# Revit family: F100G
name_source: partatom
category: Windows
revit_build: Autodesk Revit 2014 (Build: 20130308_1515(x64)
units: mm (PartAtom-declared; Revit-internal decimal feet)

## types (75) — shared parameters
Analytic Construction = <None>
Main Material = Lamilux-White
Secondary Material = Lamilux- Glass
With Operator = Yes

## per-type parameters (varying)
| type | Kurb Height | Length | Pitched Roof | Width |
| 600X600X500 | 500 mm  [stored 1.64042 ft] | 600 mm  [stored 1.9685 ft] | No | 600 mm  [stored 1.9685 ft] |
| 600X600X400 | 400 mm  [stored 1.31234 ft] | 600 mm  [stored 1.9685 ft] | No | 600 mm  [stored 1.9685 ft] |
| 600X600X300 | 300 mm  [stored 0.984252 ft] | 600 mm  [stored 1.9685 ft] | No | 600 mm  [stored 1.9685 ft] |
| 600X600X150 | 150 mm | 600 mm  [stored 1.9685 ft] | No | 600 mm  [stored 1.9685 ft] |
| 600X600X400_Pitched | 400 mm  [stored 1.31234 ft] | 600 mm  [stored 1.9685 ft] | Yes | 600 mm  [stored 1.9685 ft] |
| 600X900X500 | 500 mm  [stored 1.64042 ft] | 900 mm  [stored 2.95276 ft] | No | 600 mm  [stored 1.9685 ft] |
| 600X900X400 | 400 mm  [stored 1.31234 ft] | 900 mm  [stored 2.95276 ft] | No | 600 mm  [stored 1.9685 ft] |
| 600X900X300 | 300 mm  [stored 0.984252 ft] | 900 mm  [stored 2.95276 ft] | No | 600 mm  [stored 1.9685 ft] |
| 600X900X150 | 150 mm | 900 mm  [stored 2.95276 ft] | No | 600 mm  [stored 1.9685 ft] |
| 600X900X400_Pitched | 400 mm  [stored 1.31234 ft] | 900 mm  [stored 2.95276 ft] | Yes | 600 mm  [stored 1.9685 ft] |
| 600X1200X500 | 500 mm  [stored 1.64042 ft] | 1200 mm | No | 600 mm  [stored 1.9685 ft] |
| 600X1200X300 | 300 mm  [stored 0.984252 ft] | 1200 mm | No | 600 mm  [stored 1.9685 ft] |
| 600X1200X150 | 150 mm | 1200 mm | No | 600 mm  [stored 1.9685 ft] |
| 600X1200X400_Pitched | 400 mm  [stored 1.31234 ft] | 1200 mm | Yes | 600 mm  [stored 1.9685 ft] |
| 700X1350X500 | 500 mm  [stored 1.64042 ft] | 1350 mm  [stored 4.42913 ft] | No | 700 mm  [stored 2.29659 ft] |
| 700X1350X400 | 400 mm  [stored 1.31234 ft] | 1350 mm  [stored 4.42913 ft] | No | 700 mm  [stored 2.29659 ft] |
| 700X1350X300 | 300 mm  [stored 0.984252 ft] | 1350 mm  [stored 4.42913 ft] | No | 700 mm  [stored 2.29659 ft] |
| 700X1350X150 | 150 mm | 1350 mm  [stored 4.42913 ft] | No | 700 mm  [stored 2.29659 ft] |
| 700X1350X400_Pitched | 400 mm  [stored 1.31234 ft] | 1350 mm  [stored 4.42913 ft] | Yes | 700 mm  [stored 2.29659 ft] |
| 800X800X500 | 500 mm  [stored 1.64042 ft] | 800 mm  [stored 2.62467 ft] | No | 800 mm  [stored 2.62467 ft] |
| 800X800X400 | 400 mm  [stored 1.31234 ft] | 800 mm  [stored 2.62467 ft] | No | 800 mm  [stored 2.62467 ft] |
| 800X800X300 | 300 mm  [stored 0.984252 ft] | 800 mm  [stored 2.62467 ft] | No | 800 mm  [stored 2.62467 ft] |
| 800X800X150 | 150 mm | 800 mm  [stored 2.62467 ft] | No | 800 mm  [stored 2.62467 ft] |
| 800X800X400_Pitched | 400 mm  [stored 1.31234 ft] | 800 mm  [stored 2.62467 ft] | Yes | 800 mm  [stored 2.62467 ft] |
| 800X1500X500 | 500 mm  [stored 1.64042 ft] | 1500 mm  [stored 4.92126 ft] | No | 800 mm  [stored 2.62467 ft] |
| 800X1500X400 | 400 mm  [stored 1.31234 ft] | 1500 mm  [stored 4.92126 ft] | No | 800 mm  [stored 2.62467 ft] |
| 800X1500X300 | 300 mm  [stored 0.984252 ft] | 1500 mm  [stored 4.92126 ft] | No | 800 mm  [stored 2.62467 ft] |
| 800X1500X150 | 150 mm | 1500 mm  [stored 4.92126 ft] | No | 800 mm  [stored 2.62467 ft] |
| 800X1500X400_Pitched | 400 mm  [stored 1.31234 ft] | 1500 mm  [stored 4.92126 ft] | Yes | 800 mm  [stored 2.62467 ft] |
| 900X900X500 | 500 mm  [stored 1.64042 ft] | 900 mm  [stored 2.95276 ft] | No | 900 mm  [stored 2.95276 ft] |
| 900X900X400 | 400 mm  [stored 1.31234 ft] | 900 mm  [stored 2.95276 ft] | No | 900 mm  [stored 2.95276 ft] |
| 900X900X300 | 300 mm  [stored 0.984252 ft] | 900 mm  [stored 2.95276 ft] | No | 900 mm  [stored 2.95276 ft] |
| 900X900X150 | 150 mm | 900 mm  [stored 2.95276 ft] | No | 900 mm  [stored 2.95276 ft] |
| 900X900X400_Pitched | 400 mm  [stored 1.31234 ft] | 900 mm  [stored 2.95276 ft] | Yes | 900 mm  [stored 2.95276 ft] |
| 900X1200X500 | 500 mm  [stored 1.64042 ft] | 1200 mm | No | 900 mm  [stored 2.95276 ft] |
| 900X1200X400 | 400 mm  [stored 1.31234 ft] | 1200 mm | No | 900 mm  [stored 2.95276 ft] |
| 900X1200X300 | 300 mm  [stored 0.984252 ft] | 1200 mm | No | 900 mm  [stored 2.95276 ft] |
| 900X1200X150 | 150 mm | 1200 mm | No | 900 mm  [stored 2.95276 ft] |
| 900X1200X400_Pitched | 400 mm  [stored 1.31234 ft] | 1200 mm | Yes | 900 mm  [stored 2.95276 ft] |
| 900X1450X150 | 150 mm | 1450 mm  [stored 4.75722 ft] | No | 900 mm  [stored 2.95276 ft] |
| 900X1450X400_Pitched | 400 mm  [stored 1.31234 ft] | 1450 mm  [stored 4.75722 ft] | Yes | 900 mm  [stored 2.95276 ft] |
| 1000X1000X500 | 500 mm  [stored 1.64042 ft] | 1000 mm  [stored 3.28084 ft] | No | 1000 mm  [stored 3.28084 ft] |
| 1000X1000X400 | 400 mm  [stored 1.31234 ft] | 1000 mm  [stored 3.28084 ft] | No | 1000 mm  [stored 3.28084 ft] |
| 1000X1000X300 | 300 mm  [stored 0.984252 ft] | 1000 mm  [stored 3.28084 ft] | No | 1000 mm  [stored 3.28084 ft] |
| 1000X1000X150 | 150 mm | 1000 mm  [stored 3.28084 ft] | No | 1000 mm  [stored 3.28084 ft] |
| 1000X1000X400_Pitched | 400 mm  [stored 1.31234 ft] | 1000 mm  [stored 3.28084 ft] | Yes | 1000 mm  [stored 3.28084 ft] |
| 1000X1500X500 | 500 mm  [stored 1.64042 ft] | 1500 mm  [stored 4.92126 ft] | No | 1000 mm  [stored 3.28084 ft] |
| 1000X1500X400 | 400 mm  [stored 1.31234 ft] | 1500 mm  [stored 4.92126 ft] | No | 1000 mm  [stored 3.28084 ft] |
| 1000X1500X300 | 300 mm  [stored 0.984252 ft] | 1500 mm  [stored 4.92126 ft] | No | 1000 mm  [stored 3.28084 ft] |
| 1000X1500X150 | 150 mm | 1500 mm  [stored 4.92126 ft] | No | 1000 mm  [stored 3.28084 ft] |
| 1000X1500X400_Pitched | 400 mm  [stored 1.31234 ft] | 1500 mm  [stored 4.92126 ft] | Yes | 1000 mm  [stored 3.28084 ft] |
| 1200X1200X500 | 500 mm  [stored 1.64042 ft] | 1200 mm | No | 1200 mm |
| 1200X1200X400 | 400 mm  [stored 1.31234 ft] | 1200 mm | No | 1200 mm |
| 1200X1200X300 | 300 mm  [stored 0.984252 ft] | 1200 mm | No | 1200 mm |
| 1200X1200X150 | 150 mm | 1200 mm | No | 1200 mm |
| 1200X1200X400_Pitched | 400 mm  [stored 1.31234 ft] | 1200 mm | Yes | 1200 mm |
| 1200X1500X500 | 500 mm  [stored 1.64042 ft] | 1500 mm  [stored 4.92126 ft] | No | 1200 mm |
| 1200X1500X400 | 400 mm  [stored 1.31234 ft] | 1500 mm  [stored 4.92126 ft] | No | 1200 mm |
| 1200X1500X300 | 300 mm  [stored 0.984252 ft] | 1500 mm  [stored 4.92126 ft] | No | 1200 mm |
| 1200X1500X150 | 150 mm | 1500 mm  [stored 4.92126 ft] | No | 1200 mm |
| 1200X1500X400_Pitched | 400 mm  [stored 1.31234 ft] | 1500 mm  [stored 4.92126 ft] | Yes | 1200 mm |
| 1250X1250X500 | 500 mm  [stored 1.64042 ft] | 1250 mm  [stored 4.10105 ft] | No | 1250 mm  [stored 4.10105 ft] |
| 1250X1250X400 | 400 mm  [stored 1.31234 ft] | 1250 mm  [stored 4.10105 ft] | No | 1250 mm  [stored 4.10105 ft] |
| 1250X1250X300 | 300 mm  [stored 0.984252 ft] | 1250 mm  [stored 4.10105 ft] | No | 1250 mm  [stored 4.10105 ft] |
| 1250X1250X150 | 150 mm | 1250 mm  [stored 4.10105 ft] | No | 1250 mm  [stored 4.10105 ft] |
| 1250X1250X400_Pitched | 400 mm  [stored 1.31234 ft] | 1250 mm  [stored 4.10105 ft] | Yes | 1250 mm  [stored 4.10105 ft] |
| 1400X1400X500 | 500 mm  [stored 1.64042 ft] | 1400 mm  [stored 4.59318 ft] | No | 1400 mm  [stored 4.59318 ft] |
| 1400X1400X400 | 400 mm  [stored 1.31234 ft] | 1400 mm  [stored 4.59318 ft] | No | 1400 mm  [stored 4.59318 ft] |
| 1400X1400X300 | 300 mm  [stored 0.984252 ft] | 1400 mm  [stored 4.59318 ft] | No | 1400 mm  [stored 4.59318 ft] |
| 1400X1400X400_Pitched | 400 mm  [stored 1.31234 ft] | 1400 mm  [stored 4.59318 ft] | Yes | 1400 mm  [stored 4.59318 ft] |
| 1500X1500X500 | 500 mm  [stored 1.64042 ft] | 1500 mm  [stored 4.92126 ft] | No | 1500 mm  [stored 4.92126 ft] |
| 1500X1500X400 | 400 mm  [stored 1.31234 ft] | 1500 mm  [stored 4.92126 ft] | No | 1500 mm  [stored 4.92126 ft] |
| 1500X1500X300 | 300 mm  [stored 0.984252 ft] | 1500 mm  [stored 4.92126 ft] | No | 1500 mm  [stored 4.92126 ft] |
| 1500X1500X150 | 150 mm | 1500 mm  [stored 4.92126 ft] | No | 1500 mm  [stored 4.92126 ft] |
| 1500X1500X400_Pitched | 400 mm  [stored 1.31234 ft] | 1500 mm  [stored 4.92126 ft] | Yes | 1500 mm  [stored 4.92126 ft] |

note: [stored X ft] marks values corroborated as IEEE doubles in the binary element streams (Revit-internal decimal feet)

## geometry (parser evidence)
native form markers: Sweep x10
no freeform markers — native parametric forms only
